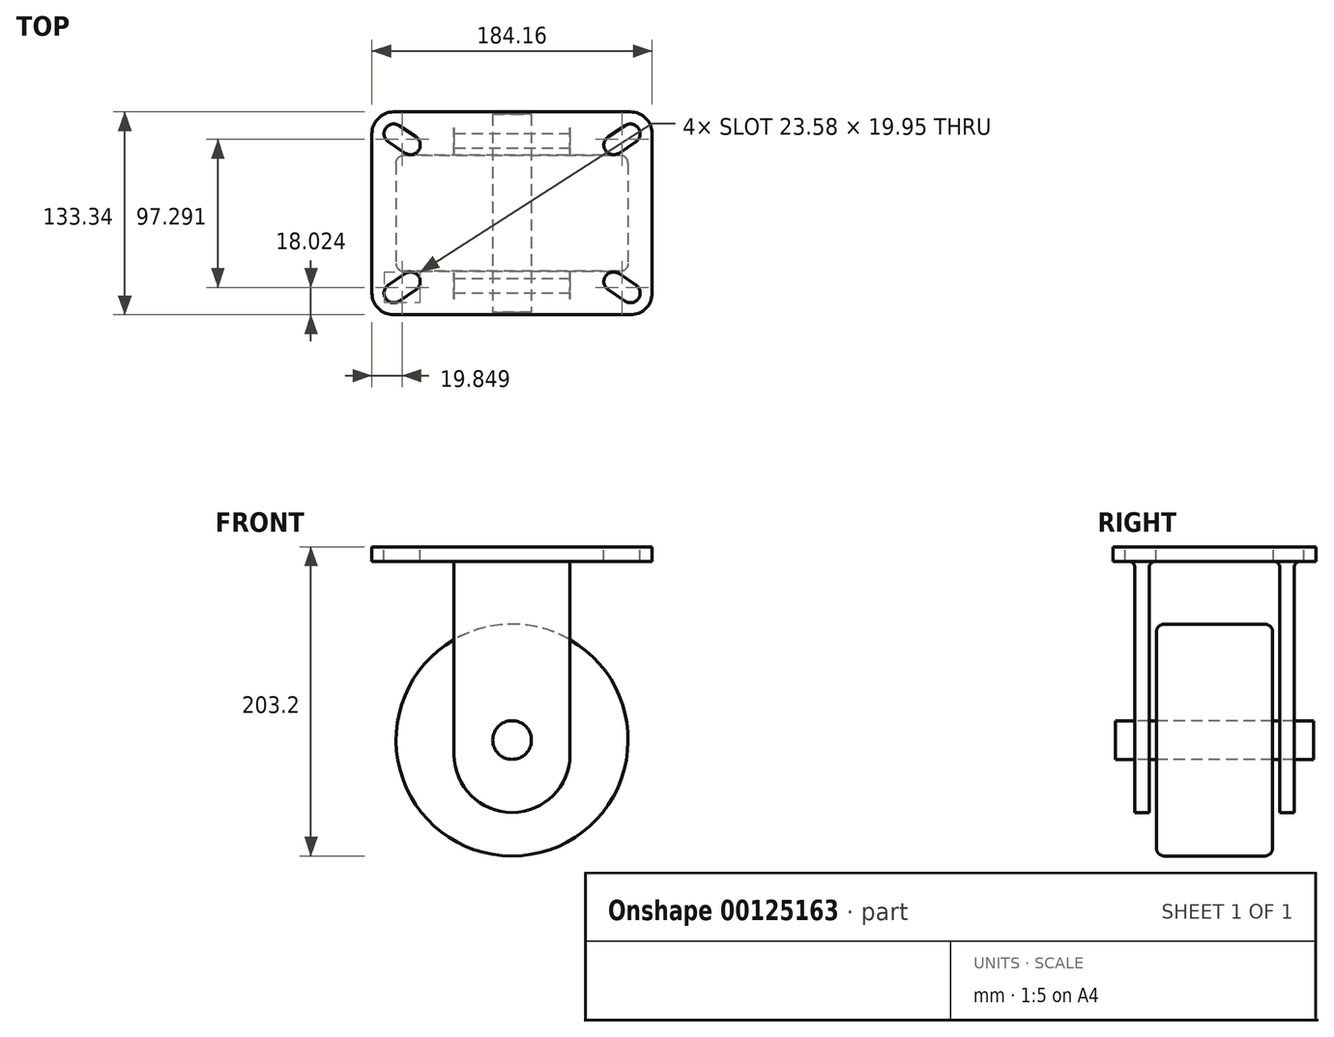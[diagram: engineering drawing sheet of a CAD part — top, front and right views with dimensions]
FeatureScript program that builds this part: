
annotation { "Feature Type Name" : "Feature", "Feature Type Description" : "" }
export const myFeature = defineFeature(function(context is Context, id is Id, definition is map)
    precondition{}
    {
        {
            var Q0;
            Q0=qCreatedBy(makeId("Top.planeOp"),FACE);
            var sketch = newSketch(context, id + "F0", { "sketchPlane" : qUnion([Q0])});
            skLineSegment(sketch, "E0.bottom", {"start": v(77.79, -66.68) * mm, "end": v(-77.79, -66.68) * mm});
            skLineSegment(sketch, "E0.top", {"start": v(77.79, 66.68) * mm, "end": v(-77.79, 66.68) * mm});
            skLineSegment(sketch, "E0.left", {"start": v(92.08, -52.39) * mm, "end": v(92.08, 52.39) * mm});
            skLineSegment(sketch, "E0.right", {"start": v(-92.08, -52.39) * mm, "end": v(-92.08, 52.39) * mm});
            skPoint(sketch, "E0.middle", {"position": v(0, 0) * mm});
            skArc(sketch, "E1", {"start": v(-77.79, 66.68) * mm, "mid": v(-87.9, 62.5) * mm, "end": v(-92.08, 52.39) * mm});
            skArc(sketch, "E2", {"start": v(92.07, 52.39) * mm, "mid": v(87.9, 62.5) * mm, "end": v(77.79, 66.68) * mm});
            skArc(sketch, "E3", {"start": v(-92.07, -52.39) * mm, "mid": v(-87.9, -62.5) * mm, "end": v(-77.79, -66.67) * mm});
            skArc(sketch, "E4", {"start": v(77.79, -66.67) * mm, "mid": v(87.9, -62.5) * mm, "end": v(92.08, -52.39) * mm});
            skPoint(sketch, "E5.orphan", {"position": v(92.08, 66.68) * mm});
            skPoint(sketch, "E6.orphan", {"position": v(92.08, -66.68) * mm});
            skPoint(sketch, "E7.orphan", {"position": v(-92.08, -66.68) * mm});
            skPoint(sketch, "E8.orphan", {"position": v(-92.08, 66.68) * mm});
            skArc(sketch, "E9", {"start": v(-74.24, 57.65) * mm, "mid": v(-83.05, 55.93) * mm, "end": v(-81.33, 47.12) * mm});
            skArc(sketch, "E10", {"start": v(81.33, 47.12) * mm, "mid": v(83.05, 55.93) * mm, "end": v(74.24, 57.65) * mm});
            skArc(sketch, "E11", {"start": v(74.24, -57.65) * mm, "mid": v(83.05, -55.93) * mm, "end": v(81.33, -47.12) * mm});
            skArc(sketch, "E12", {"start": v(-81.33, -47.12) * mm, "mid": v(-83.05, -55.93) * mm, "end": v(-74.24, -57.65) * mm});
            skArc(sketch, "E13", {"start": v(-70.22, 39.64) * mm, "mid": v(-61.4, 41.36) * mm, "end": v(-63.13, 50.17) * mm});
            skArc(sketch, "E14", {"start": v(63.13, 50.17) * mm, "mid": v(61.4, 41.36) * mm, "end": v(70.22, 39.64) * mm});
            skArc(sketch, "E15", {"start": v(-63.13, -50.17) * mm, "mid": v(-61.4, -41.36) * mm, "end": v(-70.22, -39.64) * mm});
            skArc(sketch, "E16", {"start": v(70.22, -39.64) * mm, "mid": v(61.4, -41.36) * mm, "end": v(63.13, -50.17) * mm});
            skLineSegment(sketch, "E17", {"start": v(-74.24, 57.65) * mm, "end": v(-63.13, 50.17) * mm});
            skLineSegment(sketch, "E18", {"start": v(-81.33, 47.12) * mm, "end": v(-70.22, 39.64) * mm});
            skLineSegment(sketch, "E19", {"start": v(63.13, 50.17) * mm, "end": v(74.24, 57.65) * mm});
            skLineSegment(sketch, "E20", {"start": v(70.22, 39.64) * mm, "end": v(81.33, 47.12) * mm});
            skLineSegment(sketch, "E21", {"start": v(70.22, -39.64) * mm, "end": v(81.33, -47.12) * mm});
            skLineSegment(sketch, "E22", {"start": v(63.13, -50.17) * mm, "end": v(74.24, -57.65) * mm});
            skLineSegment(sketch, "E23", {"start": v(-74.24, -57.65) * mm, "end": v(-63.13, -50.17) * mm});
            skLineSegment(sketch, "E24", {"start": v(-81.33, -47.12) * mm, "end": v(-70.22, -39.64) * mm});
            skSolve(sketch);
        }
        {
            var Q0;
            Q0=qSketchRegion(id+"F0",true);
            extrude(context, id + "F1", {"entities" : qUnion([Q0]), "oppositeDirection" : true, "depth" : 9.52 * mm});
        }
        {
            var Q0;
            Q0=qCreatedBy(makeId("Right.planeOp"),FACE);
            cPlane(context, id + "F2", {"entities" : qUnion([Q0]), "cplaneType" : CPlaneType.OFFSET, "offset" : 38.1 * mm, "width" : 152.4 * mm, "height" : 152.4 * mm});
        }
        {
            var Q0;
            Q0=qCreatedBy(id+"F2.planeOp",FACE);
            var sketch = newSketch(context, id + "F3", { "sketchPlane" : qUnion([Q0])});
            skLineSegment(sketch, "E25.0", {"start": v(-66.68, -9.53) * mm, "end": v(-66.68, 0) * mm});
            skLineSegment(sketch, "E25.1", {"start": v(-66.67, 0) * mm, "end": v(-52.39, 0) * mm});
            skLineSegment(sketch, "E25.2", {"start": v(-66.67, -9.53) * mm, "end": v(-52.39, -9.53) * mm});
            skLineSegment(sketch, "E25.3", {"start": v(-52.39, 0) * mm, "end": v(52.39, 0) * mm});
            skLineSegment(sketch, "E25.4", {"start": v(-52.39, -9.53) * mm, "end": v(52.39, -9.53) * mm});
            skLineSegment(sketch, "E25.5", {"start": v(52.39, 0) * mm, "end": v(66.68, 0) * mm});
            skLineSegment(sketch, "E25.6", {"start": v(52.39, -9.53) * mm, "end": v(66.68, -9.53) * mm});
            skLineSegment(sketch, "E25.7", {"start": v(66.68, -9.53) * mm, "end": v(66.68, 0) * mm});
            skLineSegment(sketch, "E26", {"start": v(-52.39, -13.5) * mm, "end": v(-52.39, -174.63) * mm});
            skLineSegment(sketch, "E27.0", {"start": v(-42.86, -13.5) * mm, "end": v(-42.86, -174.63) * mm});
            skArc(sketch, "E28", {"start": v(-52.39, -13.5) * mm, "mid": v(-53.55, -10.69) * mm, "end": v(-56.36, -9.53) * mm});
            skArc(sketch, "E29", {"start": v(-38.9, -9.53) * mm, "mid": v(-41.7, -10.69) * mm, "end": v(-42.86, -13.5) * mm});
            skLineSegment(sketch, "E30.MirrorCS", {"start": v(42.86, -13.5) * mm, "end": v(42.86, -174.63) * mm});
            skLineSegment(sketch, "E31.MirrorCS", {"start": v(52.39, -13.5) * mm, "end": v(52.39, -174.63) * mm});
            skArc(sketch, "E32.MirrorCS", {"start": v(38.9, -9.53) * mm, "mid": v(41.7, -10.69) * mm, "end": v(42.86, -13.5) * mm});
            skArc(sketch, "E33.MirrorCS", {"start": v(52.39, -13.5) * mm, "mid": v(53.55, -10.69) * mm, "end": v(56.36, -9.53) * mm});
            skLineSegment(sketch, "E34", {"start": v(-52.39, -174.63) * mm, "end": v(-42.86, -174.63) * mm});
            skLineSegment(sketch, "E35", {"start": v(42.86, -174.63) * mm, "end": v(52.39, -174.63) * mm});
            skSolve(sketch);
        }
        {
            var Q0;
            Q0=qSketchRegion(id+"F3",true);
            extrude(context, id + "F4", {"entities" : qUnion([Q0]), "operationType" : NewBodyOperationType.ADD, "oppositeDirection" : true, "depth" : 76.2 * mm});
        }
        {
            var Q0;
            Q0=makeQuery(id+"F4.opExtrude","SWEPT_FACE",FACE,{"disambiguationData":[OSD([sQuery(id+"F3.wireOp",EDGE,"E26")])]});
            var sketch = newSketch(context, id + "F5", { "sketchPlane" : qUnion([Q0])});
            skArc(sketch, "E36", {"start": v(-38.1, -136.53) * mm, "mid": v(0, -174.63) * mm, "end": v(38.1, -136.53) * mm});
            skPoint(sketch, "E36.first.point", {"position": v(-38.1, -136.53) * mm});
            skPoint(sketch, "E36.second.point", {"position": v(0, -174.63) * mm});
            skPoint(sketch, "E36.third.point", {"position": v(38.1, -136.53) * mm});
            skLineSegment(sketch, "E37", {"start": v(-38.1, -136.53) * mm, "end": v(-38.1, -174.63) * mm});
            skLineSegment(sketch, "E38", {"start": v(-38.1, -174.63) * mm, "end": v(38.1, -174.63) * mm});
            skLineSegment(sketch, "E39", {"start": v(38.1, -174.63) * mm, "end": v(38.1, -136.53) * mm});
            skSolve(sketch);
        }
        {
            var Q0;
            Q0=qSketchRegion(id+"F5",true);
            extrude(context, id + "F6", {"entities" : qUnion([Q0]), "operationType" : NewBodyOperationType.REMOVE, "endBound" : BoundingType.THROUGH_ALL, "oppositeDirection" : true, "depth" : 25.4 * mm});
        }
        {
            var Q0;
            Q0=qCreatedBy(makeId("Front.planeOp"),FACE);
            cPlane(context, id + "F7", {"entities" : qUnion([Q0]), "cplaneType" : CPlaneType.OFFSET, "offset" : 38.1 * mm, "width" : 152.4 * mm, "height" : 152.4 * mm});
        }
        {
            var Q0;
            Q0=qCreatedBy(id+"F7.planeOp",FACE);
            var sketch = newSketch(context, id + "F8", { "sketchPlane" : qUnion([Q0])});
            skLineSegment(sketch, "E40", {"start": v(0, 0) * mm, "end": v(0, -50.8) * mm});
            skCircle(sketch, "E41", {"center": v(0, -127) * mm, "radius": 76.2 * mm});
            skSolve(sketch);
        }
        {
            var Q0;
            Q0=qSketchRegion(id+"F8",true);
            extrude(context, id + "F9", {"entities" : qUnion([Q0]), "oppositeDirection" : true, "depth" : 76.2 * mm});
        }
        {
            var Q0;
            Q0=makeQuery(id+"F9.opExtrude","CAP_EDGE",EDGE,{"disambiguationData":[OSD([sQuery(id+"F8.wireOp",EDGE,"E41")])],"isStart":true});
            var Q1;
            Q1=makeQuery(id+"F9.opExtrude","CAP_EDGE",EDGE,{"disambiguationData":[OSD([sQuery(id+"F8.wireOp",EDGE,"E41")])],"isStart":false});
            fillet(context, id + "F10", {"entities" : qUnion([Q0, Q1]), "radius" : 5.08 * mm, "tangentPropagation" : true, "allowEdgeOverflow" : false});
        }
        {
            var Q0;
            Q0=makeQuery(id+"F4.opExtrude","SWEPT_FACE",FACE,{"disambiguationData":[OSD([sQuery(id+"F3.wireOp",EDGE,"E26")])]});
            var sketch = newSketch(context, id + "F11", { "sketchPlane" : qUnion([Q0])});
            skCircle(sketch, "E42", {"center": v(0, -127) * mm, "radius": 12.7 * mm});
            skSolve(sketch);
        }
        {
            var Q0;
            Q0=qSketchRegion(id+"F11",true);
            extrude(context, id + "F12", {"entities" : qUnion([Q0]), "oppositeDirection" : true, "depth" : 117.47 * mm, "hasSecondDirection" : true, "secondDirectionOppositeDirection" : false, "secondDirectionDepth" : 12.7 * mm});
        }
    });
